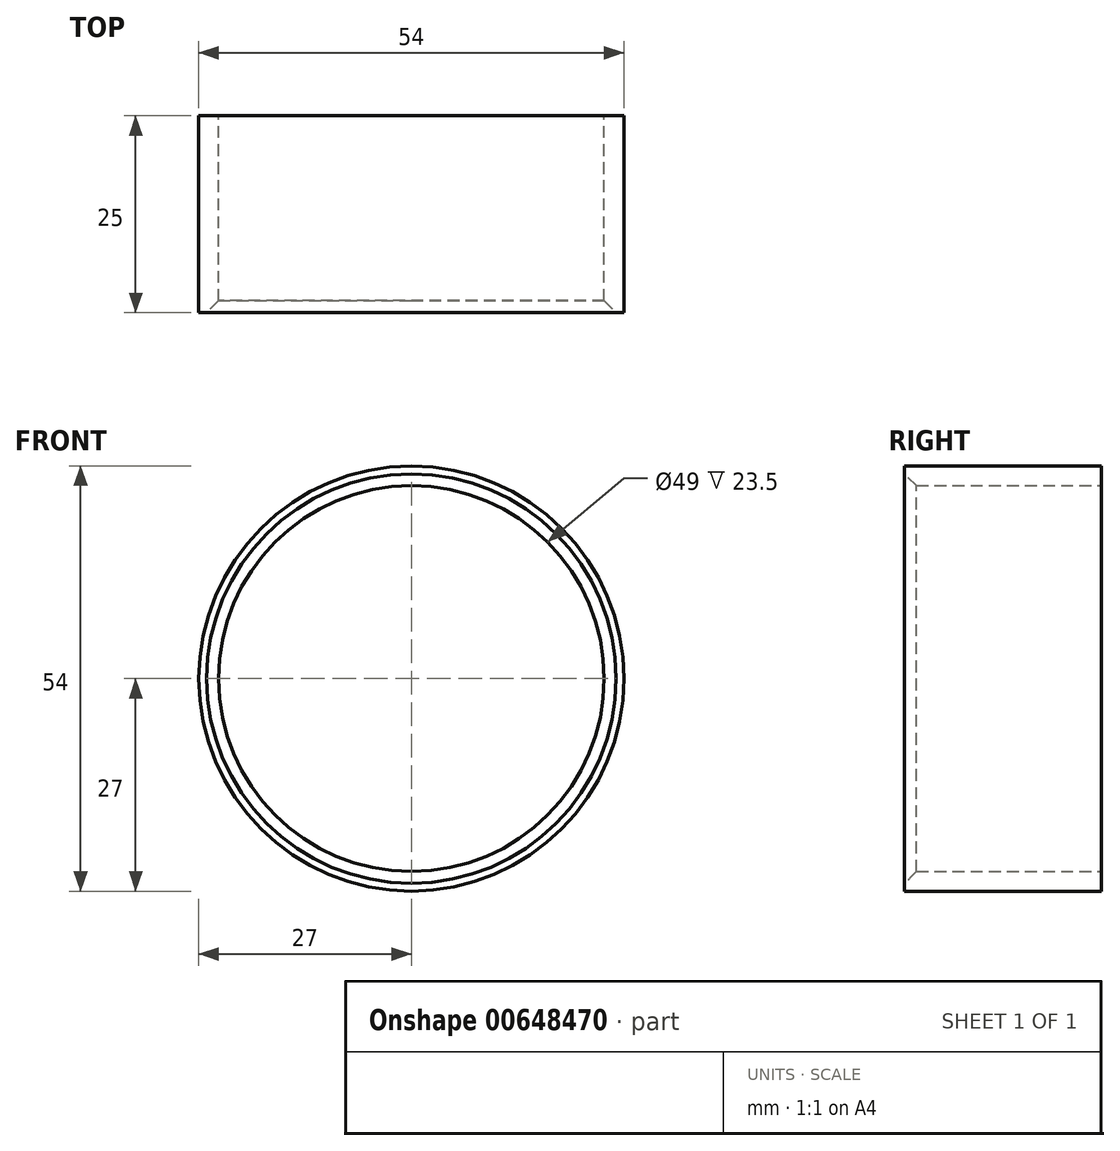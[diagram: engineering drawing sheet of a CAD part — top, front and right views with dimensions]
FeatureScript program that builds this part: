
annotation { "Feature Type Name" : "Feature", "Feature Type Description" : "" }
export const myFeature = defineFeature(function(context is Context, id is Id, definition is map)
    precondition{}
    {
        {
            var Q0;
            Q0=qCreatedBy(makeId("Front.planeOp"),FACE);
            var sketch = newSketch(context, id + "F0", { "sketchPlane" : qUnion([Q0])});
            skCircle(sketch, "E0", {"center": v(0, 0) * mm, "radius": 24.5 * mm});
            skCircle(sketch, "E1", {"center": v(0, 0) * mm, "radius": 27 * mm});
            skSolve(sketch);
        }
        {
            var Q0;
            Q0 = qSketchRegion(id + "F0", true);
            extrude(context, id + "F1", {"entities" : qUnion([Q0]), "depth" : 25 * mm, "offsetDistance" : 25 * mm});
        }
        {
            var Q0;
            Q0=makeQuery(id+"F1.opExtrude","CAP_EDGE",EDGE,{"disambiguationData":[OSD([sQuery(id+"F0.wireOp",EDGE,"E0")])],"isStart":false});
            chamfer(context, id + "F2", {"entities" : qUnion([Q0]), "chamferType" : ChamferType.OFFSET_ANGLE, "width" : 1.5 * mm, "oppositeDirection" : false, "angle" : 45 * degree, "tangentPropagation" : true});
        }
    });
